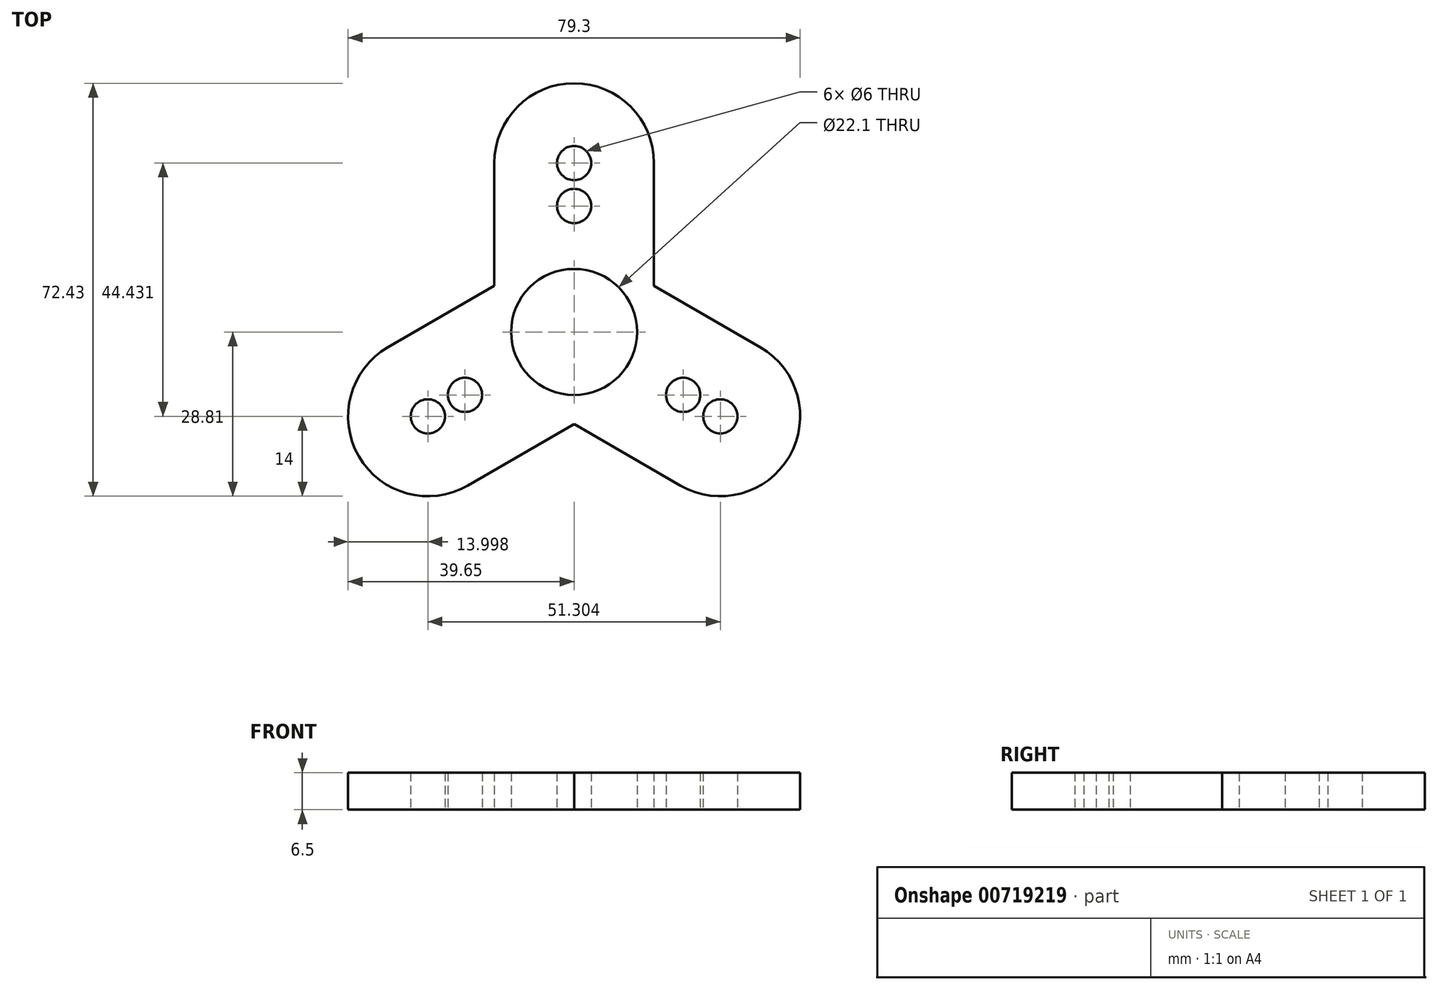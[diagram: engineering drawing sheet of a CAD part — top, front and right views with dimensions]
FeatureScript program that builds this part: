
annotation { "Feature Type Name" : "Feature", "Feature Type Description" : "" }
export const myFeature = defineFeature(function(context is Context, id is Id, definition is map)
    precondition{}
    {
        {
            var Q0;
            Q0=qCreatedBy(makeId("Top.planeOp"),FACE);
            var sketch = newSketch(context, id + "F0", { "sketchPlane" : qUnion([Q0])});
            skCircle(sketch, "E0", {"center": v(0, 0) * mm, "radius": 11.05 * mm});
            skCircle(sketch, "E1", {"center": v(0, 0) * mm, "radius": 14 * mm});
            skCircle(sketch, "E2", {"center": v(0, 29.62) * mm, "radius": 14 * mm});
            skLineSegment(sketch, "E3", {"start": v(-14, 0) * mm, "end": v(-14, 30) * mm});
            skLineSegment(sketch, "E4", {"start": v(14, 0) * mm, "end": v(14, 30) * mm});
            skCircle(sketch, "E5", {"center": v(0, 29.62) * mm, "radius": 3 * mm});
            skCircle(sketch, "E6", {"center": v(0, 22.1) * mm, "radius": 3 * mm});
            skCircle(sketch, "E7.1.0", {"center": v(-19.14, -11.05) * mm, "radius": 3 * mm});
            skCircle(sketch, "E7.2.0", {"center": v(19.14, -11.05) * mm, "radius": 3 * mm});
            skLineSegment(sketch, "E8.1.0", {"start": v(7, -12.12) * mm, "end": v(-18.98, -27.12) * mm});
            skLineSegment(sketch, "E8.2.0", {"start": v(7, 12.12) * mm, "end": v(32.98, -2.88) * mm});
            skLineSegment(sketch, "E9.1.0", {"start": v(-7, 12.12) * mm, "end": v(-32.98, -2.88) * mm});
            skLineSegment(sketch, "E9.2.0", {"start": v(-7, -12.12) * mm, "end": v(18.98, -27.12) * mm});
            skCircle(sketch, "E10.1.0", {"center": v(-25.65, -14.81) * mm, "radius": 14 * mm});
            skCircle(sketch, "E10.2.0", {"center": v(25.65, -14.81) * mm, "radius": 14 * mm});
            skCircle(sketch, "E11.1.0", {"center": v(-25.65, -14.81) * mm, "radius": 3 * mm});
            skCircle(sketch, "E11.2.0", {"center": v(25.65, -14.81) * mm, "radius": 3 * mm});
            skSolve(sketch);
        }
        {
            var Q0;
            Q0=makeQuery(id+"F0.imprint","IMPRINT",FACE,{"disambiguationData":[TD([[makeQuery(id+"F0.imprint","IMPRINT",EDGE,{"derivedFrom":sQuery(id+"F0.wireOp",EDGE,"E7.1.0")}),-1.0]])]});
            var Q1;
            {var subQ3=sQuery(id+"F0.wireOp",EDGE,"E3");var subQ9=sQuery(id+"F0.wireOp",EDGE,"E1");var subQ10=makeQuery(id+"F0.imprint","INTERSECT",VERTEX,{"derivedFrom":[subQ9,subQ3]});Q1=makeQuery(id+"F0.imprint","IMPRINT",FACE,{"disambiguationData":[TD([[makeQuery(id+"F0.imprint","IMPRINT",EDGE,{"disambiguationData":[TD([[subQ10,-1.0]])],"derivedFrom":subQ9}),-1.0]])]});}
            var Q2;
            {var subQ0=sQuery(id+"F0.wireOp",EDGE,"E8.1.0");var subQ1=sQuery(id+"F0.wireOp",EDGE,"E1");var subQ2=makeQuery(id+"F0.imprint","INTERSECT",VERTEX,{"derivedFrom":[subQ1,subQ0]});Q2=makeQuery(id+"F0.imprint","IMPRINT",FACE,{"disambiguationData":[TD([[makeQuery(id+"F0.imprint","IMPRINT",EDGE,{"disambiguationData":[TD([[subQ2,1.0]])],"derivedFrom":subQ1}),-1.0]])]});}
            var Q3;
            Q3=makeQuery(id+"F0.imprint","IMPRINT",FACE,{"disambiguationData":[TD([[makeQuery(id+"F0.imprint","IMPRINT",EDGE,{"derivedFrom":sQuery(id+"F0.wireOp",EDGE,"E7.2.0")}),-1.0]])]});
            var Q4;
            {var subQ3=sQuery(id+"F0.wireOp",EDGE,"E4");var subQ6=sQuery(id+"F0.wireOp",EDGE,"E1");var subQ10=makeQuery(id+"F0.imprint","INTERSECT",VERTEX,{"derivedFrom":[subQ6,subQ3]});Q4=makeQuery(id+"F0.imprint","IMPRINT",FACE,{"disambiguationData":[TD([[makeQuery(id+"F0.imprint","IMPRINT",EDGE,{"disambiguationData":[TD([[subQ10,1.0]])],"derivedFrom":subQ6}),-1.0]])]});}
            var Q5;
            Q5=makeQuery(id+"F0.imprint","IMPRINT",FACE,{"disambiguationData":[TD([[makeQuery(id+"F0.imprint","IMPRINT",EDGE,{"derivedFrom":sQuery(id+"F0.wireOp",EDGE,"E5")}),-1.0]])]});
            var Q6;
            {var subQ5=sQuery(id+"F0.wireOp",EDGE,"E1");var subQ9=sQuery(id+"F0.wireOp",EDGE,"E8.2.0");var subQ10=makeQuery(id+"F0.imprint","INTERSECT",VERTEX,{"derivedFrom":[subQ5,subQ9]});Q6=makeQuery(id+"F0.imprint","IMPRINT",FACE,{"disambiguationData":[TD([[makeQuery(id+"F0.imprint","IMPRINT",EDGE,{"disambiguationData":[TD([[subQ10,-1.0]])],"derivedFrom":subQ5}),-1.0]])]});}
            var Q7;
            {var subQ0=sQuery(id+"F0.wireOp",EDGE,"E3");var subQ1=sQuery(id+"F0.wireOp",EDGE,"E1");var subQ2=makeQuery(id+"F0.imprint","INTERSECT",VERTEX,{"derivedFrom":[subQ1,subQ0]});Q7=makeQuery(id+"F0.imprint","IMPRINT",FACE,{"disambiguationData":[TD([[makeQuery(id+"F0.imprint","IMPRINT",EDGE,{"disambiguationData":[TD([[subQ2,1.0]])],"derivedFrom":subQ1}),-1.0]])]});}
            var Q8;
            Q8=makeQuery(id+"F0.imprint","IMPRINT",FACE,{"disambiguationData":[TD([[makeQuery(id+"F0.imprint","IMPRINT",EDGE,{"derivedFrom":sQuery(id+"F0.wireOp",EDGE,"E0")}),-1.0]])]});
            var Q9;
            {var subQ0=sQuery(id+"F0.wireOp",EDGE,"E4");var subQ1=sQuery(id+"F0.wireOp",EDGE,"E1");var subQ2=makeQuery(id+"F0.imprint","INTERSECT",VERTEX,{"derivedFrom":[subQ1,subQ0]});Q9=makeQuery(id+"F0.imprint","IMPRINT",FACE,{"disambiguationData":[TD([[makeQuery(id+"F0.imprint","IMPRINT",EDGE,{"disambiguationData":[TD([[subQ2,-1.0]])],"derivedFrom":subQ1}),-1.0]])]});}
            extrude(context, id + "F1", {"entities" : qUnion([Q0, Q1, Q2, Q3, Q4, Q5, Q6, Q7, Q8, Q9]), "depth" : 6.5 * mm, "offsetDistance" : 25 * mm});
        }
    });
